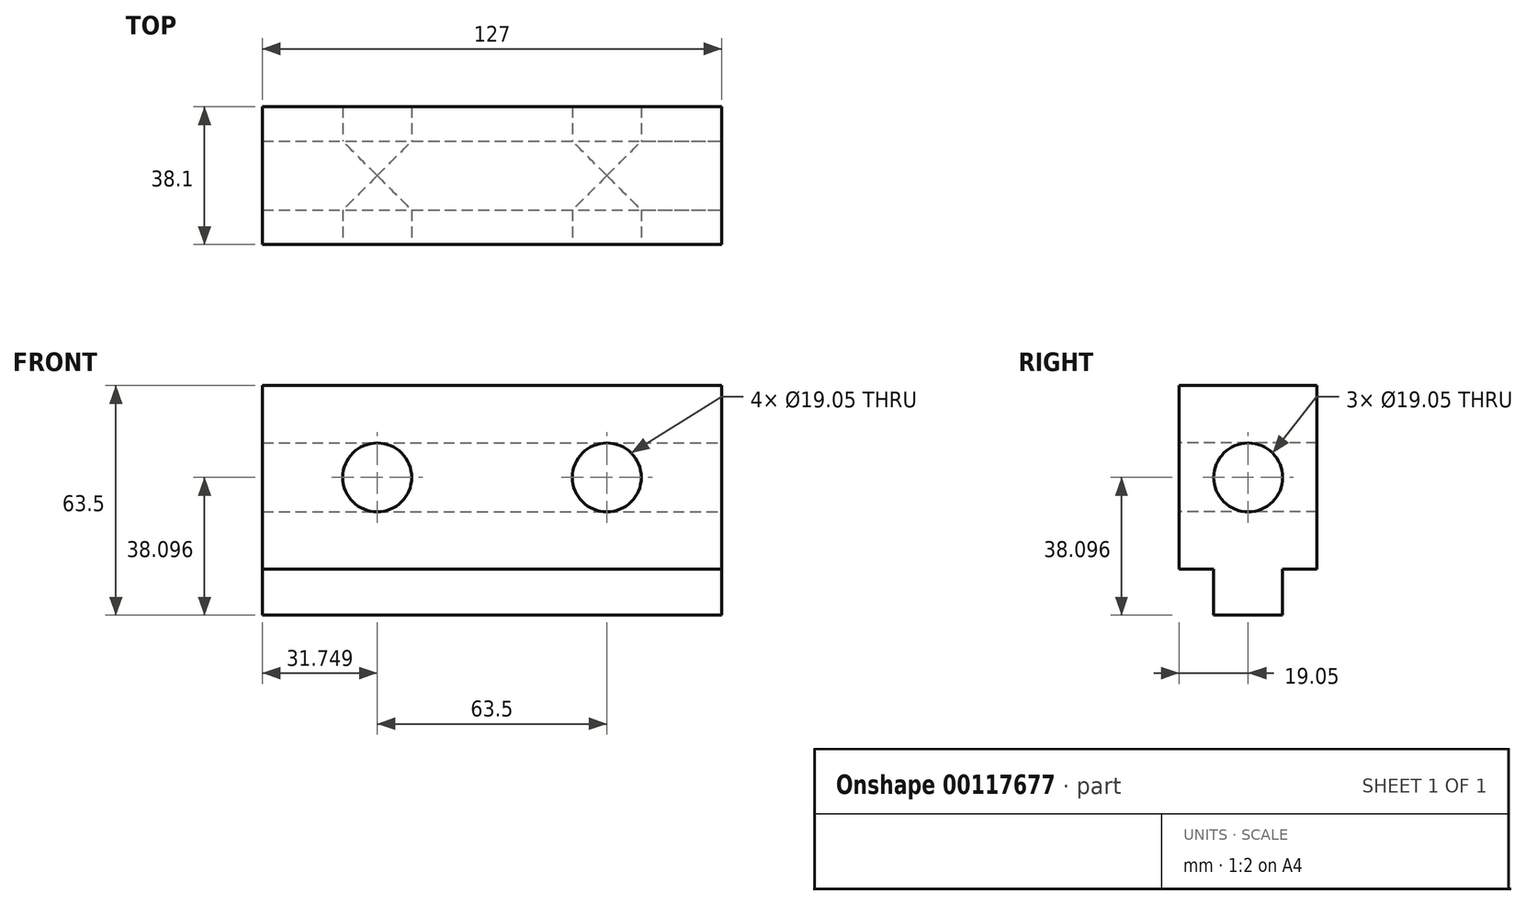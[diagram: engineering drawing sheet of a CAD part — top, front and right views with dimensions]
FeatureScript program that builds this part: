
annotation { "Feature Type Name" : "Feature", "Feature Type Description" : "" }
export const myFeature = defineFeature(function(context is Context, id is Id, definition is map)
    precondition{}
    {
        {
            var Q0;
            Q0=qCreatedBy(makeId("Front.planeOp"),FACE);
            var sketch = newSketch(context, id + "F0", { "sketchPlane" : qUnion([Q0])});
            skLineSegment(sketch, "E0.bottom", {"start": v(-77.74, 21.1) * mm, "end": v(49.26, 21.1) * mm});
            skLineSegment(sketch, "E0.top", {"start": v(-77.74, -42.4) * mm, "end": v(49.26, -42.4) * mm});
            skLineSegment(sketch, "E0.left", {"start": v(-77.74, 21.1) * mm, "end": v(-77.74, -42.4) * mm});
            skLineSegment(sketch, "E0.right", {"start": v(49.26, 21.1) * mm, "end": v(49.26, -42.4) * mm});
            skSolve(sketch);
        }
        {
            var Q0;
            Q0 = qSketchRegion(id + "F0", true);
            extrude(context, id + "F1", {"entities" : qUnion([Q0]), "depth" : 38.1 * mm});
        }
        {
            var Q0;
            Q0=makeQuery(id+"F1.opExtrude","SWEPT_FACE",FACE,{"disambiguationData":[OSD([sQuery(id+"F0.wireOp",EDGE,"E0.right")])]});
            var sketch = newSketch(context, id + "F2", { "sketchPlane" : qUnion([Q0])});
            skLineSegment(sketch, "E1.bottom", {"start": v(-38.1, -42.4) * mm, "end": v(-28.57, -42.4) * mm});
            skLineSegment(sketch, "E1.top", {"start": v(-38.1, -29.7) * mm, "end": v(-28.58, -29.7) * mm});
            skLineSegment(sketch, "E1.left", {"start": v(-38.1, -42.4) * mm, "end": v(-38.1, -29.7) * mm});
            skLineSegment(sketch, "E1.right", {"start": v(-28.57, -42.4) * mm, "end": v(-28.58, -29.7) * mm});
            skSolve(sketch);
        }
        {
            var Q0;
            Q0 = qSketchRegion(id + "F2", true);
            extrude(context, id + "F3", {"entities" : qUnion([Q0]), "operationType" : NewBodyOperationType.REMOVE, "oppositeDirection" : true, "depth" : 127 * mm});
        }
        {
            var Q0;
            Q0=makeQuery(id+"F1.opExtrude","SWEPT_FACE",FACE,{"disambiguationData":[OSD([sQuery(id+"F0.wireOp",EDGE,"E0.right")])]});
            var sketch = newSketch(context, id + "F4", { "sketchPlane" : qUnion([Q0])});
            skLineSegment(sketch, "E2.bottom", {"start": v(0, -42.4) * mm, "end": v(-9.53, -42.4) * mm});
            skLineSegment(sketch, "E2.top", {"start": v(0, -29.7) * mm, "end": v(-9.53, -29.7) * mm});
            skLineSegment(sketch, "E2.left", {"start": v(0, -42.4) * mm, "end": v(0, -29.7) * mm});
            skLineSegment(sketch, "E2.right", {"start": v(-9.53, -42.4) * mm, "end": v(-9.53, -29.7) * mm});
            skSolve(sketch);
        }
        {
            var Q0;
            Q0 = qSketchRegion(id + "F4", true);
            extrude(context, id + "F5", {"entities" : qUnion([Q0]), "operationType" : NewBodyOperationType.REMOVE, "oppositeDirection" : true, "depth" : 127 * mm});
        }
        {
            var Q0;
            Q0=makeQuery(id+"F1.opExtrude","SWEPT_FACE",FACE,{"disambiguationData":[OSD([sQuery(id+"F0.wireOp",EDGE,"E0.right")])]});
            var sketch = newSketch(context, id + "F6", { "sketchPlane" : qUnion([Q0])});
            skCircle(sketch, "E3", {"center": v(-19.05, -4.3) * mm, "radius": 9.53 * mm});
            skSolve(sketch);
        }
        {
            var Q0;
            Q0 = qSketchRegion(id + "F6", true);
            extrude(context, id + "F7", {"entities" : qUnion([Q0]), "operationType" : NewBodyOperationType.REMOVE, "oppositeDirection" : true, "depth" : 127 * mm});
        }
        {
            var Q0;
            Q0=makeQuery(id+"F1.opExtrude","CAP_FACE",FACE,{"disambiguationData":[OSD([sQuery(id+"F0.wireOp",EDGE,"E0.bottom"),sQuery(id+"F0.wireOp",EDGE,"E0.top"),sQuery(id+"F0.wireOp",EDGE,"E0.left"),sQuery(id+"F0.wireOp",EDGE,"E0.right")])],"isStart":false});
            var sketch = newSketch(context, id + "F8", { "sketchPlane" : qUnion([Q0])});
            skCircle(sketch, "E4", {"center": v(-46, -4.3) * mm, "radius": 9.53 * mm});
            skCircle(sketch, "E5", {"center": v(17.5, -4.3) * mm, "radius": 9.53 * mm});
            skSolve(sketch);
        }
        {
            var Q0;
            Q0 = qSketchRegion(id + "F8", true);
            extrude(context, id + "F9", {"entities" : qUnion([Q0]), "operationType" : NewBodyOperationType.REMOVE, "oppositeDirection" : true, "depth" : 38.1 * mm});
        }
    });
